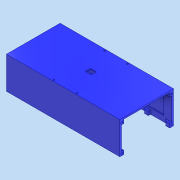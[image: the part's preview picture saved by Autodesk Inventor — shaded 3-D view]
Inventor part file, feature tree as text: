
AUTODESK INVENTOR PART (.ipt)
format: ipt  version: 2022 (Build 260153000, 153)  size: 407,552 bytes
history: native  units: in
note: dims shown in document units (in); Inventor stores cm internally (conversion verified against a paired STEP export)
features: extrude x16, sketch x16, projected_geometry x9, chamfer x2
ambient origin geometry x8: Origin, YZ Plane, XZ Plane, XY Plane, X Axis, Y Axis, Z Axis, Center Point
bodies: Solid1 (feature_tree)
feature tree (43):
  extrude  "Extrusion1"  Depth=5.1969in
  extrude  "Extrusion2"  Depth=0.1575in
  extrude  "Extrusion3"  Depth=0.2362in
  extrude  "Extrusion4"  Depth=0.3937in
  extrude  "Extrusion5"  Depth=0.1575in
  extrude  "Extrusion6"  Depth=2.6772in
  extrude  "Extrusion7"  Depth=0.3937in
  extrude  "Extrusion8"  Depth=0.3937in TaperAngle=0.0deg
  extrude  "Extrusion9"  Depth=0.3937in TaperAngle=0.0deg
  extrude  "Extrusion10"  Depth=0.2362in TaperAngle=0.0deg
  extrude  "Extrusion11"  Depth=0.1575in
  chamfer  "Chamfer4"  Distance=0.1575in
  extrude  "Extrusion13"  Depth=0.1969in
  extrude  "Extrusion14"  Depth=0.2362in TaperAngle=0.0deg
  chamfer  "Chamfer5"  Distance=0.2362in
  extrude  "Extrusion15"  Depth=0.2362in TaperAngle=0.0deg
  extrude  "Extrusion16"  Depth=2.3622in
  extrude  "Extrusion18"  Depth=0.1575in
  sketch  "Sketch1"  dims[d0=11.4961in d1=5.1969in]
  sketch  "Sketch2"  dims[d2=0.1575in d3=0.1575in]
  sketch  "Sketch3"  dims[d4=3.1496in d5=0.0in d6=0.2362in]
  sketch  "Sketch4"  dims[d7=2.2047in d8=0.3937in]
  sketch  "Sketch6"  dims[d9=0.3937in d10=0.0in d11=0.1575in]
  sketch  "Sketch7"  dims[d12=0.1181in d13=2.6772in]
  sketch  "Sketch8"  dims[d14=0.3937in d15=0.0in d16=0.3937in]
  sketch  "Sketch11"  dims[d17=0.2362in d18=0.3937in d19=0.0in]
  sketch  "Sketch12"  dims[d20=0.3937in d21=0.3937in d22=0.0in]
  projected_geometry  "Projected Loop3"
  projected_geometry  "Projected Loop4"
  sketch  "Sketch13"  dims[d23=0.1969in d24=0.2362in d25=0.0in]
  projected_geometry  "Projected Loop5"
  projected_geometry  "Projected Loop6"
  sketch  "Sketch14"  dims[d26=1.2598in d27=0.1181in d28=0.1575in d29=0.0in]
  projected_geometry  "Projected Loop7"
  projected_geometry  "Projected Loop8"
  projected_geometry  "Projected Loop9"
  projected_geometry  "Projected Loop10"
  sketch  "Sketch16"  dims[d39=0.1969in d40=0.1969in]
  sketch  "Sketch17"  dims[d41=0.1969in d42=0.2362in d43=0.0in d44=0.2362in d45=0.0in]
  sketch  "Sketch18"  dims[d46=0.2362in d47=0.0in d48=0.2362in d49=0.0in]
  sketch  "Sketch19"  dims[d50=0.2362in d51=0.3937in d52=45.0deg d79=2.3622in]
  sketch  "Sketch20"  dims[d80=5.1969in d81=0.1575in d82=0.1378in d83=0.1575in d84=0.0in d85=0.5906in d86=0.5118in d87=0.1575in d88=0.1575in d89=0.315in d90=0.1575in d91=0.0in d92=0.4724in d93=0.1575in d94=0.1575in d95=0.1575in d96=0.0787in d97=45.0deg d98=0.1969in d99=0.3937in d100=0.0787in d101=0.0in d102=0.1969in d103=0.1969in d104=0.1969in d105=0.1969in d106=0.0787in d107=0.0in d110=0.0787in d111=0.0in d30=0.0197in d31=0.0344in d32=0.0197in d33=0.0344in]
  projected_geometry  "Projected Loop11"
